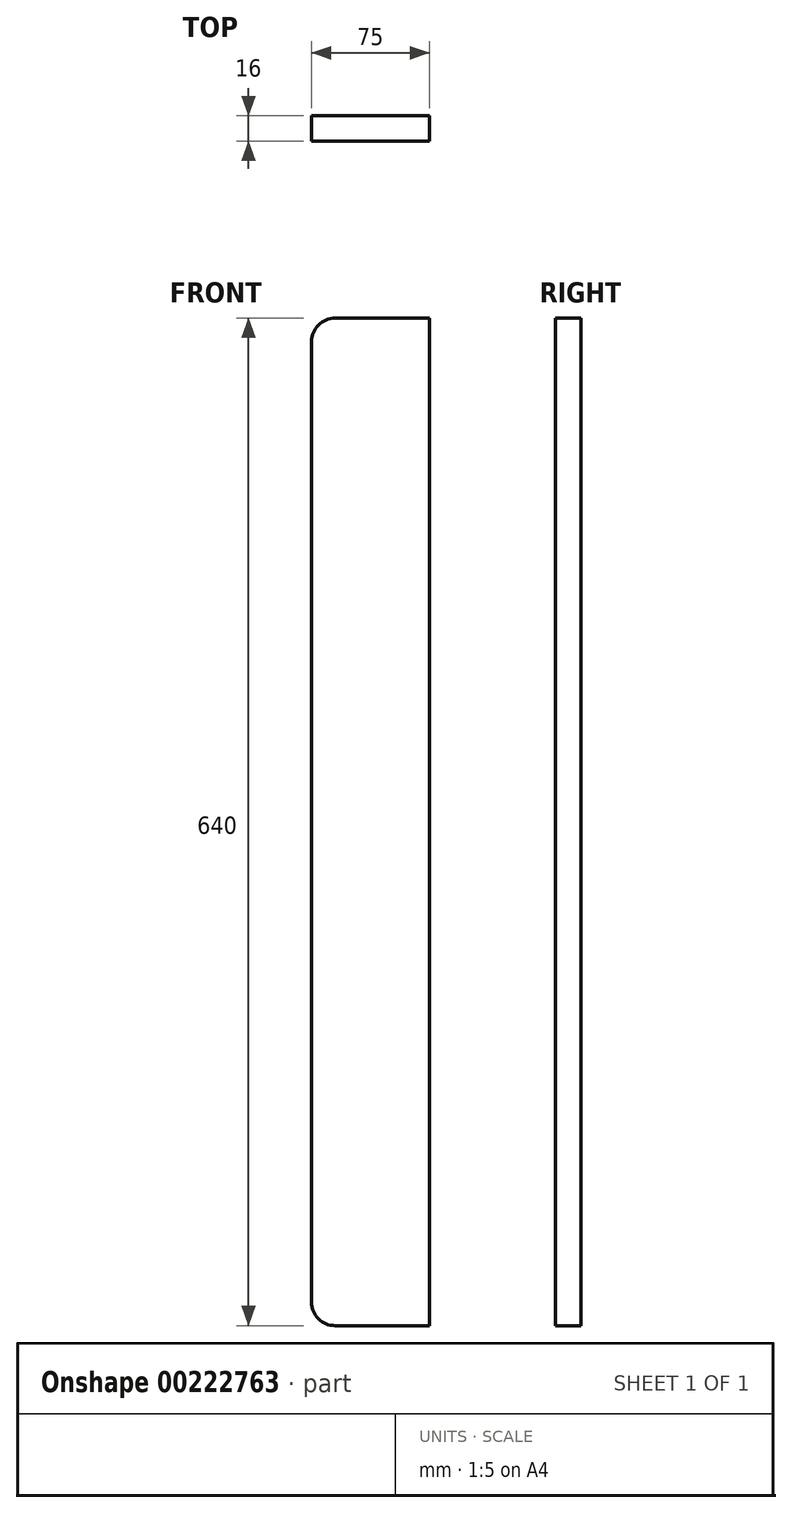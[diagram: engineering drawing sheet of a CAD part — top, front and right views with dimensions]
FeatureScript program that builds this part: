
annotation { "Feature Type Name" : "Feature", "Feature Type Description" : "" }
export const myFeature = defineFeature(function(context is Context, id is Id, definition is map)
    precondition{}
    {
        {
            var Q0;
            Q0=qCreatedBy(makeId("Front.planeOp"),FACE);
            var sketch = newSketch(context, id + "F0", { "sketchPlane" : qUnion([Q0])});
            skLineSegment(sketch, "E0.bottom", {"start": v(15, 640) * mm, "end": v(75, 640) * mm});
            skLineSegment(sketch, "E0.top", {"start": v(15, 0) * mm, "end": v(75, 0) * mm});
            skLineSegment(sketch, "E0.left", {"start": v(0, 625) * mm, "end": v(0, 15) * mm});
            skPoint(sketch, "E1.visualSharp", {"position": v(0, 640) * mm});
            skArc(sketch, "E1.filletArc", {"start": v(15, 640) * mm, "mid": v(4.4, 635.6) * mm, "end": v(0, 625) * mm});
            skPoint(sketch, "E2.visualSharp", {"position": v(0, 0) * mm});
            skArc(sketch, "E2.filletArc", {"start": v(0, 15) * mm, "mid": v(4.4, 4.4) * mm, "end": v(15, 0) * mm});
            skLineSegment(sketch, "E3", {"start": v(75, 640) * mm, "end": v(75, 0) * mm});
            skLineSegment(sketch, "E4", {"start": v(0, 285.28) * mm, "end": v(75, 285.28) * mm, "construction": true});
            skSolve(sketch);
        }
        {
            var Q0;
            Q0=makeQuery(id+"F0.imprint","IMPRINT",FACE,{"disambiguationData":[TD([[makeQuery(id+"F0.imprint","IMPRINT",EDGE,{"derivedFrom":sQuery(id+"F0.wireOp",EDGE,"E0.bottom")}),-1.0]])]});
            extrude(context, id + "F1", {"entities" : qUnion([Q0]), "depth" : 16 * mm});
        }
    });
